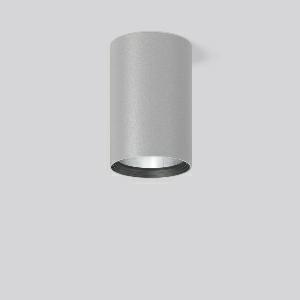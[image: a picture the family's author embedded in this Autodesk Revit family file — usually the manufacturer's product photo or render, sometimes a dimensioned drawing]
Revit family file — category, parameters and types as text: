
# Revit family: heledon_maxi_a_931219_004_3_76_6b73
name_source: partatom
category: Lighting Fixtures
units: mm (PartAtom-declared; Revit-internal decimal feet)

## family parameters
Cut with Voids When Loaded = No
Host = Face
Light Source = No
Part Type = Normal
Room Calculation Point = No
Round Connector Dimension = Use Diameter
Shared = No

## types (1)
- HELEDON maxi A (1 x LED Modul 935, 3250 lm, 3500)
    Apparent Load = 25 VA
    Approval mark = CE
    CIE Flux Codes = 97 100 100 100 100
    Color Rendering = 92
    Color Temperature = 3500
    Default Elevation = 1800 mm
    Description = Series: HELEDON maxi
Cylindrical surface-mounted downlight. Housing: die-cast aluminium, powder-coated. Internal ceiling frame polycarbonate with bayonet mounting. Black plastic ring and recessed LED to prevent glare from the side. Optical assembly with reflector made of MIRO-Silver with 98% total light reflection for outstanding efficiency - can be changed without tools. Best colour rendering index Ra>90. Suitable for Ceiling mounting. Easy installation with a separate ceiling frame with bayonet mounting and plug connection. Driver integrated. Connected via plug-in connector. High quality converter without flickering and stroboscopic effect. The following accessories can be mounted without use of tools: interchangeable lenses, decorative glasses, honeycomb louvre, clear and frosted diffusers, white interchangeable plastic ring. 
Colour: silver
Diameter: 123 mm
Height: 183 mm
Lamp: LED
Socket: without socket
Colour temperature: 3500K
Colour rendering index (CRI): 92
System power: 25 W
Rated luminous flux: 3250 lm
Luminous efficiency: 130 lm/W
Control gear: Converter, dimmable, DALI
Protection class: I
Type of protection: IP 20
    Height = 183 mm
    Lamp = 1 x LED Modul 935
    Lamp Light Flux = 3250 lm
    Lamp count = 1
    Length = 123 mm
    Lifetime = 50000 h
    Luminous efficacy = 130 lm/W
    Manufacturer = RZB
    ModVariant = No
    Model = 931219.004.3.76
    Mounting Place = Ceiling
    Mounting Type = Surface mounted
    Number of Poles = 1
    OnlyDefault = Yes
    Power Factor = 1
    Product Name = HELEDON maxi A
    Product group = Surface mounted downlights
    ProductGroupID = 302
    Protection Class = Protection class I
    Protection Degree = IP 20
    RLX_Detail_Level = 1
    RLX_Emergency_Light_Flux = 0 lm
    RLX_Emergency_Type = 0
    RLX_Emergency_Type_DB = No
    RlxData = <blob elided: 98421 chars, md5=880dd491>
    Socket = socket
    Standby Power = 0 W
    System Light Flux = 3250 lm
    System Power = 25 W
    Type Comments = Product without accessories
    Type Image = 931192.004.jpg
    URL = http://relux.com
    VarID = ---
    Voltage = 230 V
    Voltage Range = 220-240 V
    Weight = 0.00 kg
    Width = 0 mm  [stored 0 ft]

note: [stored X ft] marks values corroborated as IEEE doubles in the binary element streams (Revit-internal decimal feet)

## geometry (parser evidence)
native form markers: Blend x4, Sweep x9
no freeform markers — native parametric forms only
